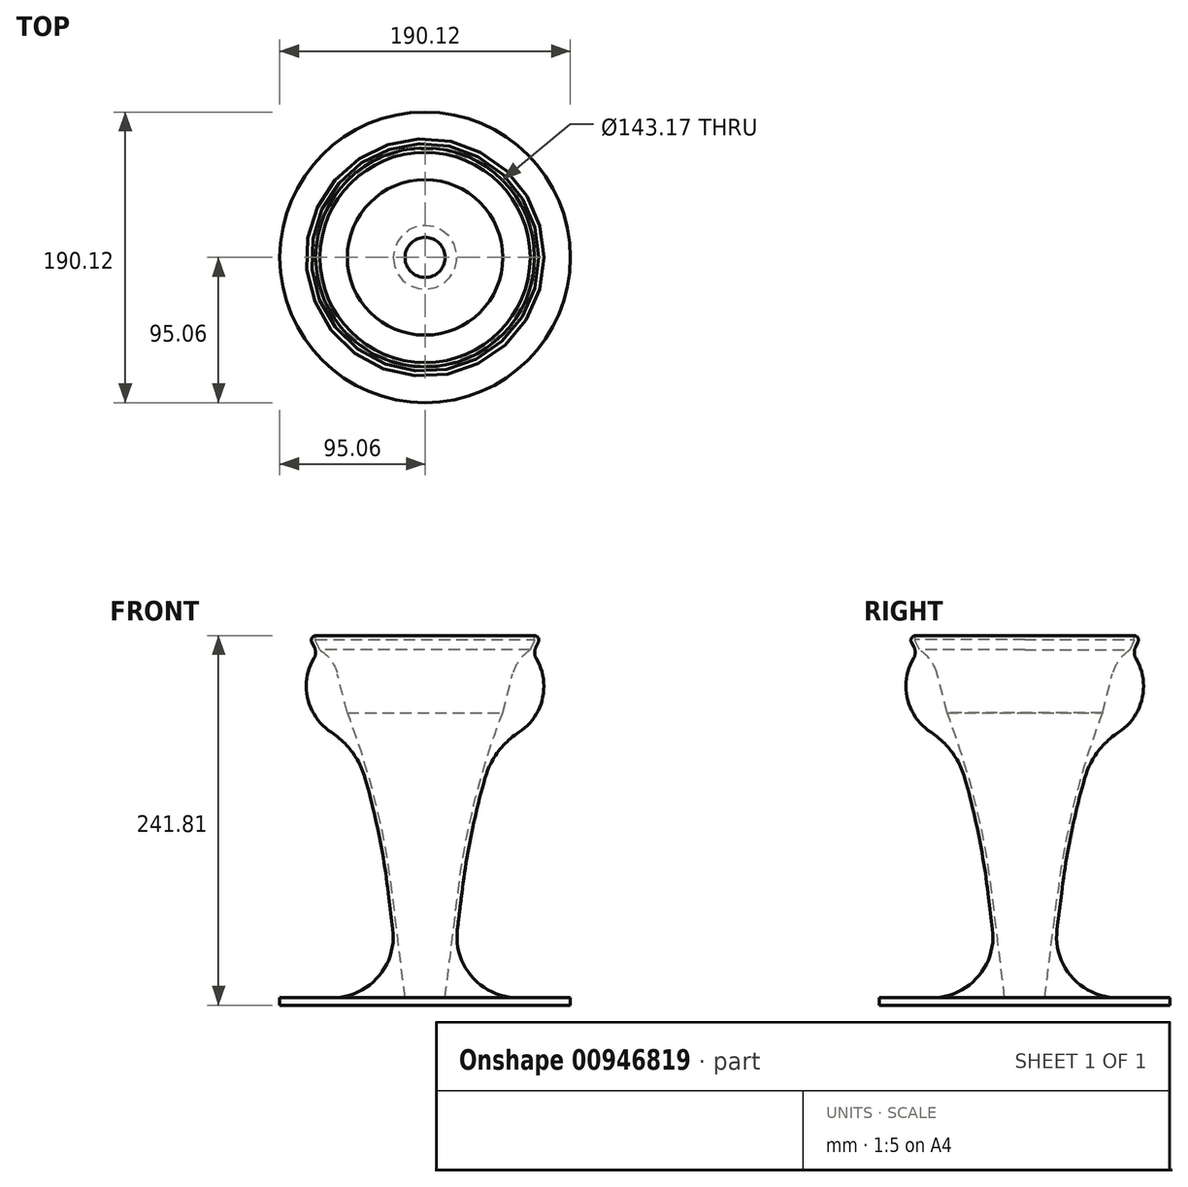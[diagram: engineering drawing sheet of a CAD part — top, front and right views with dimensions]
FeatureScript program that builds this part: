
annotation { "Feature Type Name" : "Feature", "Feature Type Description" : "" }
export const myFeature = defineFeature(function(context is Context, id is Id, definition is map)
    precondition{}
    {
        {
            var Q0;
            Q0=qCreatedBy(makeId("Top.planeOp"),FACE);
            cPlane(context, id + "F0", {"entities" : qUnion([Q0]), "cplaneType" : CPlaneType.OFFSET, "offset" : 130.05 * mm, "width" : 152.4 * mm, "height" : 152.4 * mm});
        }
        {
            var Q0;
            Q0=qCreatedBy(makeId("Top.planeOp"),FACE);
            cPlane(context, id + "F1", {"entities" : qUnion([Q0]), "cplaneType" : CPlaneType.OFFSET, "offset" : 43.43 * mm, "width" : 152.4 * mm, "height" : 152.4 * mm});
        }
        {
            var Q0;
            Q0=qCreatedBy(id+"F0.planeOp",FACE);
            var sketch = newSketch(context, id + "F2", { "sketchPlane" : qUnion([Q0])});
            skCircle(sketch, "E0", {"center": v(0, 0) * mm, "radius": 76.17 * mm});
            skSolve(sketch);
        }
        {
            var Q0;
            Q0=qCreatedBy(id+"F1.planeOp",FACE);
            var sketch = newSketch(context, id + "F3", { "sketchPlane" : qUnion([Q0])});
            skCircle(sketch, "E1", {"center": v(0, 0) * mm, "radius": 34 * mm});
            skSolve(sketch);
        }
        {
            var Q0;
            Q0=qCreatedBy(makeId("Top.planeOp"),FACE);
            cPlane(context, id + "F4", {"entities" : qUnion([Q0]), "cplaneType" : CPlaneType.OFFSET, "offset" : 33.02 * mm, "oppositeDirection" : true, "width" : 152.4 * mm, "height" : 152.4 * mm});
        }
        {
            var Q0;
            Q0=makeQuery(id+"F2.imprint","IMPRINT",FACE,{"disambiguationData":[TD([[makeQuery(id+"F2.imprint","IMPRINT",EDGE,{"derivedFrom":sQuery(id+"F2.wireOp",EDGE,"E0")}),1.0]])]});
            var Q1;
            Q1=makeQuery(id+"F3.imprint","IMPRINT",FACE,{"disambiguationData":[TD([[makeQuery(id+"F3.imprint","IMPRINT",EDGE,{"derivedFrom":sQuery(id+"F3.wireOp",EDGE,"E1")}),1.0]])]});
            loft(context, id + "F5", {"sheetProfilesArray" : [{ "sheetProfileEntities" : qUnion([Q0]) }, { "sheetProfileEntities" : qUnion([Q1]) }]});
        }
        {
            var Q0;
            Q0=qCreatedBy(id+"F4.planeOp",FACE);
            cPlane(context, id + "F6", {"entities" : qUnion([Q0]), "cplaneType" : CPlaneType.OFFSET, "offset" : 78.74 * mm, "oppositeDirection" : true, "width" : 152.4 * mm, "height" : 152.4 * mm});
        }
        {
            var Q0;
            Q0=qCreatedBy(id+"F6.planeOp",FACE);
            var sketch = newSketch(context, id + "F7", { "sketchPlane" : qUnion([Q0])});
            skCircle(sketch, "E2", {"center": v(0, 0) * mm, "radius": 15.1 * mm});
            skSolve(sketch);
        }
        {
            var Q1;
            Q1=makeQuery(id+"F5.opLoft","CAP_FACE",FACE,{"disambiguationData":[OSD([makeQuery(id+"F3.imprint","IMPRINT",FACE,{"disambiguationData":[TD([[makeQuery(id+"F3.imprint","IMPRINT",EDGE,{"derivedFrom":sQuery(id+"F3.wireOp",EDGE,"E1")}),1.0]])]})])],"isStart":true});
            var Q2;
            Q2=makeQuery(id+"F7.imprint","IMPRINT",FACE,{"disambiguationData":[TD([[makeQuery(id+"F7.imprint","IMPRINT",EDGE,{"derivedFrom":sQuery(id+"F7.wireOp",EDGE,"E2")}),1.0]])]});
            loft(context, id + "F8", {"operationType" : NewBodyOperationType.ADD, "sheetProfilesArray" : [{ "sheetProfileEntities" : qUnion([Q1]) }, { "sheetProfileEntities" : qUnion([Q2]) }]});
        }
        {
            var Q0;
            {var subQ0=sQuery(id+"F3.wireOp",EDGE,"E1");Q0=makeQuery(id+"F8.boolean.opBoolean","MERGE",EDGE,{"derivedFrom":[makeQuery(id+"F5.opLoft","MID_CAP_EDGE",EDGE,{"disambiguationData":[OSD([subQ0])],"capPos":1.0}),makeQuery(id+"F8.opLoft","MID_CAP_EDGE",EDGE,{"disambiguationData":[OSD([subQ0])],"capPos":0.0})]});}
            fillet(context, id + "F9", {"entities" : qUnion([Q0]), "radius" : 492.3 * mm, "tangentPropagation" : true, "allowEdgeOverflow" : false});
        }
        {
            var Q0;
            Q0=makeQuery(id+"F5.opLoft","MID_CAP_EDGE",EDGE,{"disambiguationData":[OSD([sQuery(id+"F2.wireOp",EDGE,"E0")])],"capPos":0.0});
            fillet(context, id + "F10", {"entities" : qUnion([Q0]), "radius" : 2.87 * mm, "tangentPropagation" : true, "allowEdgeOverflow" : false});
        }
        {
            var Q0;
            Q0=makeQuery(id+"F5.opLoft","CAP_FACE",FACE,{"disambiguationData":[OSD([makeQuery(id+"F2.imprint","IMPRINT",FACE,{"disambiguationData":[TD([[makeQuery(id+"F2.imprint","IMPRINT",EDGE,{"derivedFrom":sQuery(id+"F2.wireOp",EDGE,"E0")}),1.0]])]})])],"isStart":true});
            shell(context, id + "F11", {"entities" : qUnion([Q0]), "thickness" : 2.54 * mm});
        }
        {
            var Q0;
            Q0=makeQuery(id+"F8.opLoft","CAP_FACE",FACE,{"disambiguationData":[OSD([makeQuery(id+"F7.imprint","IMPRINT",FACE,{"disambiguationData":[TD([[makeQuery(id+"F7.imprint","IMPRINT",EDGE,{"derivedFrom":sQuery(id+"F7.wireOp",EDGE,"E2")}),1.0]])]})])],"isStart":true});
            var sketch = newSketch(context, id + "F12", { "sketchPlane" : qUnion([Q0])});
            skCircle(sketch, "E3", {"center": v(0, 0) * mm, "radius": 95.06 * mm});
            skSolve(sketch);
        }
        {
            var Q0;
            Q0 = qSketchRegion(id + "F12", true);
            extrude(context, id + "F13", {"entities" : qUnion([Q0]), "operationType" : NewBodyOperationType.ADD, "oppositeDirection" : true, "depth" : 4.83 * mm, "offsetDistance" : 25.4 * mm});
        }
        {
            var Q0;
            Q0=makeQuery(id+"F8.opLoft","MID_CAP_EDGE",EDGE,{"disambiguationData":[OSD([sQuery(id+"F7.wireOp",EDGE,"E2")])],"capPos":1.0});
            var Q1;
            Q1=makeQuery(id+"F13.boolean.opBoolean","INTERSECT",EDGE,{"derivedFrom":[makeQuery(id+"F8.opLoft","SWEPT_FACE",FACE,{"disambiguationData":[OSD([sQuery(id+"F3.wireOp",EDGE,"E1"),sQuery(id+"F7.wireOp",EDGE,"E2")])]}),makeQuery(id+"F13.opExtrude","CAP_FACE",FACE,{"disambiguationData":[OSD([sQuery(id+"F12.wireOp",EDGE,"E3")])],"isStart":false})]});
            fillet(context, id + "F14", {"entities" : qUnion([Q0, Q1]), "radius" : 39.97 * mm, "tangentPropagation" : true, "allowEdgeOverflow" : false});
        }
        {
            var Q0;
            Q0=qCreatedBy(makeId("Right.planeOp"),FACE);
            var sketch = newSketch(context, id + "F15", { "sketchPlane" : qUnion([Q0])});
            skLineSegment(sketch, "E4", {"start": v(-62.8, 126.15) * mm, "end": v(-46.12, 61.27) * mm});
            skArc(sketch, "E5", {"start": v(-62.8, 126.15) * mm, "mid": v(-76.59, 88.02) * mm, "end": v(-46.12, 61.27) * mm});
            skSolve(sketch);
        }
        {
            var Q0;
            Q0=makeQuery(id+"F15.imprint","IMPRINT",FACE,{"disambiguationData":[TD([[makeQuery(id+"F15.imprint","IMPRINT",EDGE,{"derivedFrom":sQuery(id+"F15.wireOp",EDGE,"E4")}),-1.0]])]});
            var Q1;
            Q1=makeQuery(id+"F13.opExtrude","CAP_EDGE",EDGE,{"disambiguationData":[OSD([sQuery(id+"F12.wireOp",EDGE,"E3")])],"isStart":false});
            revolve(context, id + "F16", {"operationType" : NewBodyOperationType.ADD, "surfaceOperationType" : NewSurfaceOperationType.NEW, "entities" : qUnion([Q0]), "axis" : qUnion([Q1]), "revolveType" : RevolveType.FULL});
        }
        {
            var Q0;
            Q0=makeQuery(id+"F16.boolean.opBoolean","INTERSECT",EDGE,{"derivedFrom":[makeQuery(id+"F9.opFillet","BLEND_FACE",FACE,{"disambiguationData":[OSD([sQuery(id+"F3.wireOp",EDGE,"E1")])]}),makeQuery(id+"F16.opRevolve","SWEPT_FACE",FACE,{"disambiguationData":[OSD([sQuery(id+"F15.wireOp",EDGE,"E5")])]})]});
            fillet(context, id + "F17", {"entities" : qUnion([Q0]), "radius" : 53.15 * mm, "tangentPropagation" : true, "allowEdgeOverflow" : false});
        }
        {
            var Q0;
            {var subQ0=sQuery(id+"F15.wireOp",EDGE,"E5");var subQ1=sQuery(id+"F15.wireOp",EDGE,"E4");Q0=makeQuery(id+"F16.opRevolve","SWEPT_EDGE",EDGE,{"disambiguationData":[OSD([subQ1,subQ0]),TDD([makeQuery(id+"F15.imprint","INTERSECT",VERTEX,{"disambiguationData":[OD(0.0)],"derivedFrom":[subQ1,subQ0]})])]});}
            fillet(context, id + "F18", {"entities" : qUnion([Q0]), "radius" : 26.56 * mm, "tangentPropagation" : true, "allowEdgeOverflow" : false});
        }
        {
            var Q0;
            Q0=makeQuery(id+"F16.boolean.opBoolean","INTERSECT",EDGE,{"derivedFrom":[makeQuery(id+"F5.opLoft","SWEPT_FACE",FACE,{"disambiguationData":[OSD([sQuery(id+"F2.wireOp",EDGE,"E0"),sQuery(id+"F3.wireOp",EDGE,"E1")])]}),makeQuery(id+"F16.opRevolve","SWEPT_FACE",FACE,{"disambiguationData":[OSD([sQuery(id+"F15.wireOp",EDGE,"E5")])]})]});
            fillet(context, id + "F19", {"entities" : qUnion([Q0]), "radius" : 7.4 * mm, "tangentPropagation" : true, "allowEdgeOverflow" : false});
        }
    });
